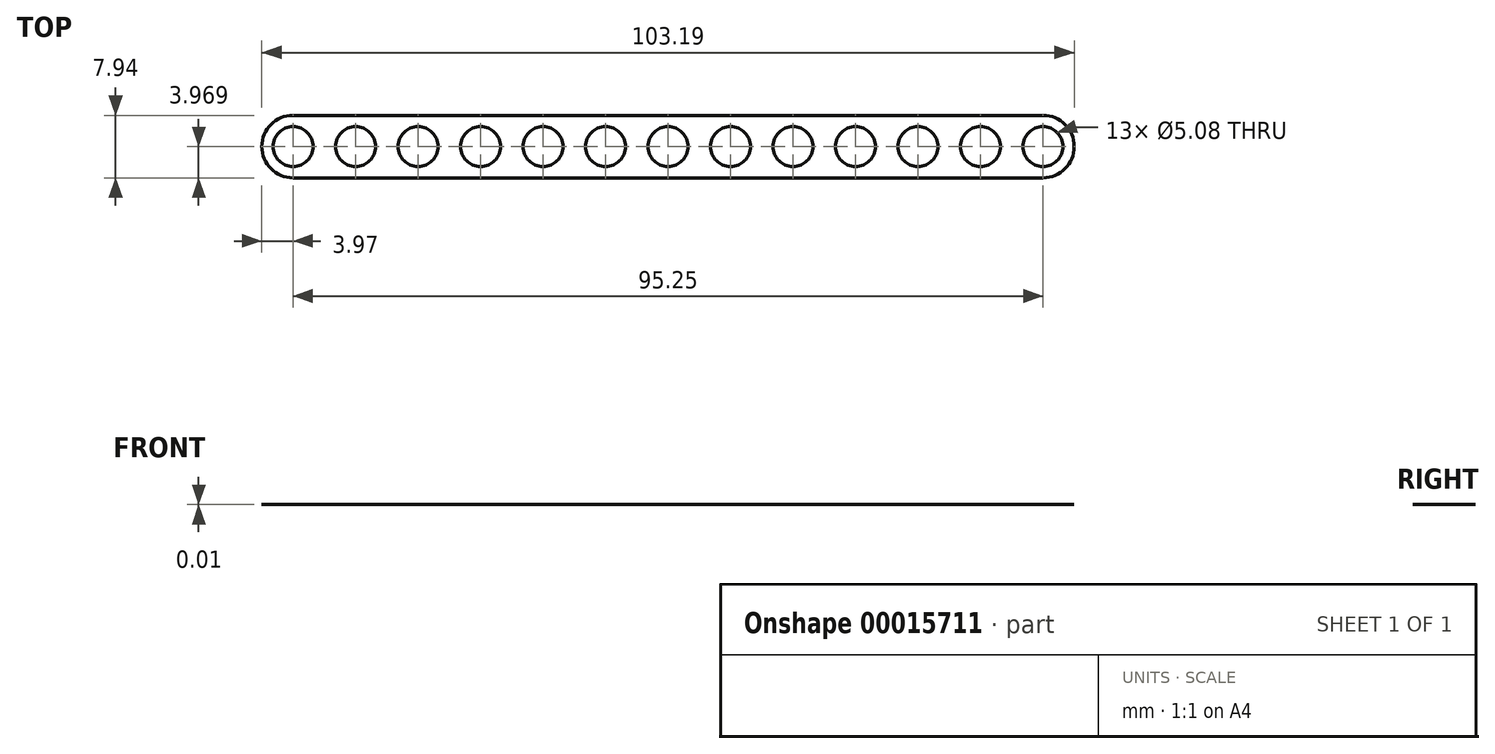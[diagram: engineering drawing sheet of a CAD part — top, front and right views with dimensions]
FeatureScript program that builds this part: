
annotation { "Feature Type Name" : "Feature", "Feature Type Description" : "" }
export const myFeature = defineFeature(function(context is Context, id is Id, definition is map)
    precondition{}
    {
        {
            var Q0;
            Q0=qCreatedBy(makeId("Top.planeOp"),FACE);
            var sketch = newSketch(context, id + "F0", { "sketchPlane" : qUnion([Q0])});
            skLineSegment(sketch, "E0.bottom", {"start": v(0, 0) * mm, "end": v(95.25, 0) * mm});
            skLineSegment(sketch, "E0.top", {"start": v(0, 7.94) * mm, "end": v(95.25, 7.94) * mm});
            skLineSegment(sketch, "E0.left", {"start": v(0, 0) * mm, "end": v(0, 7.94) * mm});
            skLineSegment(sketch, "E0.right", {"start": v(95.25, 0) * mm, "end": v(95.25, 7.94) * mm});
            skLineSegment(sketch, "E1", {"start": v(7.94, 3.97) * mm, "end": v(15.88, 3.97) * mm});
            skCircle(sketch, "E2", {"center": v(15.88, 3.97) * mm, "radius": 2.54 * mm});
            skCircle(sketch, "E3", {"center": v(7.94, 3.97) * mm, "radius": 2.54 * mm});
            skCircle(sketch, "E4", {"center": v(0, 3.97) * mm, "radius": 2.54 * mm});
            skLineSegment(sketch, "E5", {"start": v(7.94, 3.97) * mm, "end": v(0, 3.97) * mm});
            skArc(sketch, "E6", {"start": v(95.25, 0) * mm, "mid": v(99.22, 3.97) * mm, "end": v(95.25, 7.94) * mm});
            skArc(sketch, "E7", {"start": v(0, 7.94) * mm, "mid": v(-3.97, 3.97) * mm, "end": v(0, 0) * mm});
            skLineSegment(sketch, "E8", {"start": v(15.88, 3.97) * mm, "end": v(23.81, 3.97) * mm, "construction": true});
            skLineSegment(sketch, "E9", {"start": v(23.81, 3.97) * mm, "end": v(31.75, 3.97) * mm, "construction": true});
            skLineSegment(sketch, "E10", {"start": v(31.75, 3.97) * mm, "end": v(39.69, 3.97) * mm, "construction": true});
            skLineSegment(sketch, "E11", {"start": v(39.69, 3.97) * mm, "end": v(47.62, 3.97) * mm, "construction": true});
            skLineSegment(sketch, "E12", {"start": v(47.62, 3.97) * mm, "end": v(55.56, 3.97) * mm, "construction": true});
            skLineSegment(sketch, "E13", {"start": v(55.56, 3.97) * mm, "end": v(63.5, 3.97) * mm, "construction": true});
            skLineSegment(sketch, "E14", {"start": v(63.5, 3.97) * mm, "end": v(71.44, 3.97) * mm, "construction": true});
            skLineSegment(sketch, "E15", {"start": v(71.44, 3.97) * mm, "end": v(79.38, 3.97) * mm, "construction": true});
            skLineSegment(sketch, "E16", {"start": v(79.38, 3.97) * mm, "end": v(87.31, 3.97) * mm, "construction": true});
            skLineSegment(sketch, "E17", {"start": v(87.31, 3.97) * mm, "end": v(95.25, 3.97) * mm, "construction": true});
            skCircle(sketch, "E18", {"center": v(23.81, 3.97) * mm, "radius": 2.54 * mm});
            skCircle(sketch, "E19", {"center": v(31.75, 3.97) * mm, "radius": 2.54 * mm});
            skCircle(sketch, "E20", {"center": v(39.69, 3.97) * mm, "radius": 2.54 * mm});
            skCircle(sketch, "E21", {"center": v(47.62, 3.97) * mm, "radius": 2.54 * mm});
            skCircle(sketch, "E22", {"center": v(55.56, 3.97) * mm, "radius": 2.54 * mm});
            skCircle(sketch, "E23", {"center": v(63.5, 3.97) * mm, "radius": 2.54 * mm});
            skCircle(sketch, "E24", {"center": v(71.44, 3.97) * mm, "radius": 2.54 * mm});
            skCircle(sketch, "E25", {"center": v(79.38, 3.97) * mm, "radius": 2.54 * mm});
            skCircle(sketch, "E26", {"center": v(87.31, 3.97) * mm, "radius": 2.54 * mm});
            skCircle(sketch, "E27", {"center": v(95.25, 3.97) * mm, "radius": 2.54 * mm});
            skSolve(sketch);
        }
        {
            var Q0;
            Q0=qSketchRegion(id+"F0",true);
            extrude(context, id + "F1", {"entities" : qUnion([Q0]), "depth" : 5 / 406.4 * mm});
        }
    });
